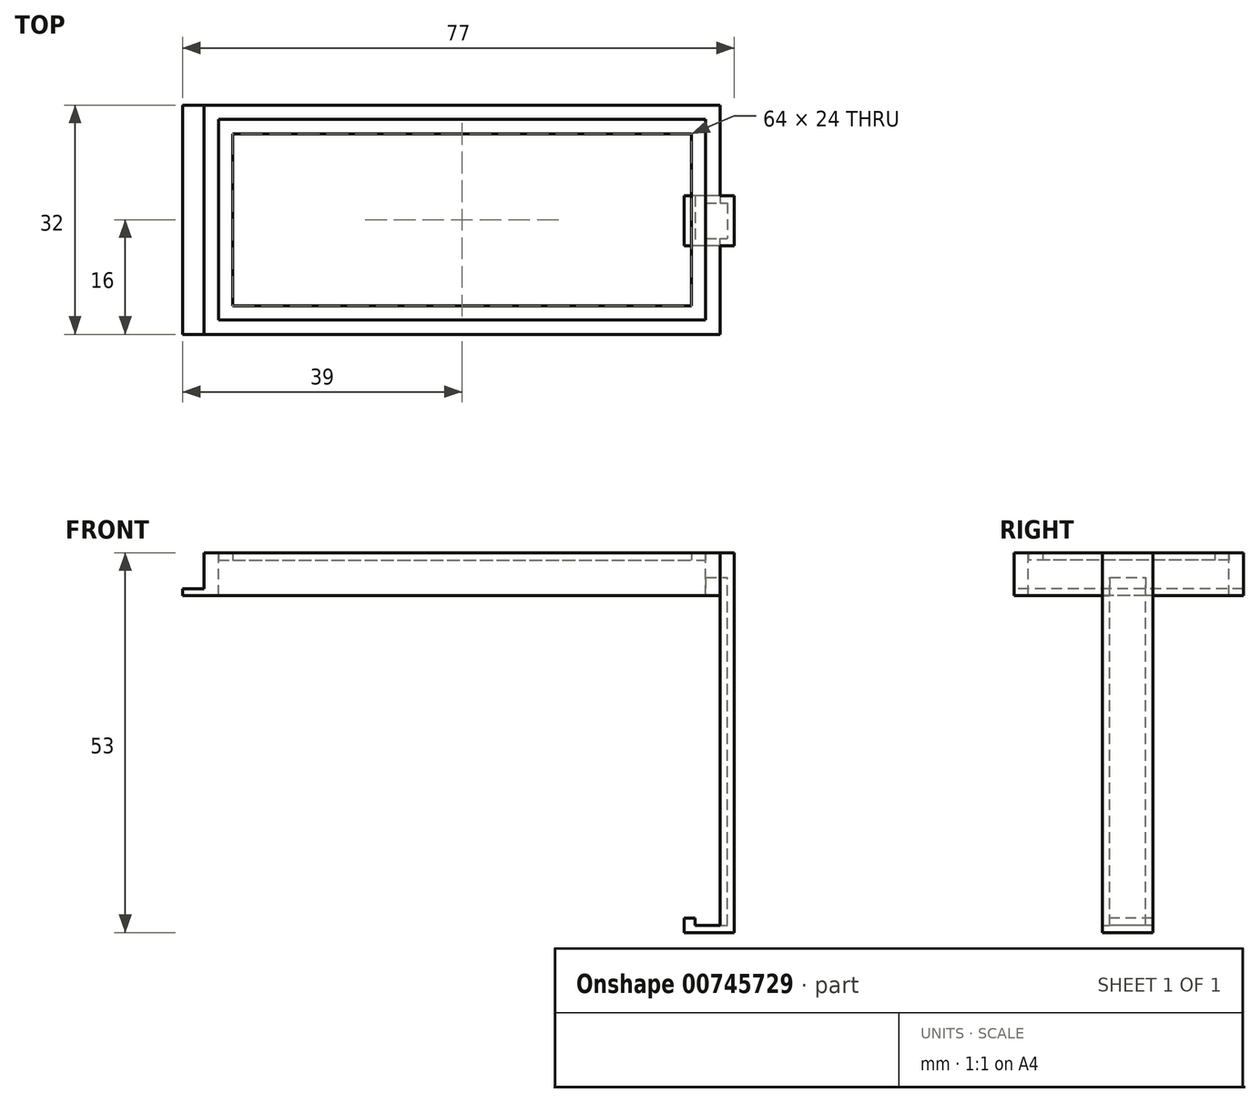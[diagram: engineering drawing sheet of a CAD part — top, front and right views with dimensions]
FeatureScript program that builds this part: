
annotation { "Feature Type Name" : "Feature", "Feature Type Description" : "" }
export const myFeature = defineFeature(function(context is Context, id is Id, definition is map)
    precondition{}
    {
        {
            var Q0;
            Q0=qCreatedBy(makeId("Top.planeOp"),FACE);
            var sketch = newSketch(context, id + "F0", { "sketchPlane" : qUnion([Q0])});
            skLineSegment(sketch, "E0.bottom", {"start": v(-32, 12) * mm, "end": v(32, 12) * mm});
            skLineSegment(sketch, "E0.top", {"start": v(-32, -12) * mm, "end": v(32, -12) * mm});
            skLineSegment(sketch, "E0.left", {"start": v(-32, 12) * mm, "end": v(-32, -12) * mm});
            skLineSegment(sketch, "E0.right", {"start": v(32, 12) * mm, "end": v(32, -12) * mm});
            skPoint(sketch, "E0.middle", {"position": v(0, 0) * mm});
            skLineSegment(sketch, "E1.0", {"start": v(-34, 14) * mm, "end": v(34, 14) * mm});
            skLineSegment(sketch, "E1.1", {"start": v(-34, 14) * mm, "end": v(-34, -14) * mm});
            skLineSegment(sketch, "E1.2", {"start": v(-34, -14) * mm, "end": v(34, -14) * mm});
            skLineSegment(sketch, "E1.3", {"start": v(34, 14) * mm, "end": v(34, -14) * mm});
            skSolve(sketch);
        }
        {
            var Q0;
            Q0=makeQuery(id+"F0.imprint","IMPRINT",FACE,{"disambiguationData":[TD([[makeQuery(id+"F0.imprint","IMPRINT",EDGE,{"derivedFrom":sQuery(id+"F0.wireOp",EDGE,"E0.bottom")}),1.0]])]});
            extrude(context, id + "F1", {"entities" : qUnion([Q0]), "depth" : 1 * mm, "offsetDistance" : 25 * mm});
        }
        {
            var Q0;
            Q0=makeQuery(id+"F1.opExtrude","CAP_FACE",FACE,{"disambiguationData":[OSD([sQuery(id+"F0.wireOp",EDGE,"E0.bottom"),sQuery(id+"F0.wireOp",EDGE,"E0.top"),sQuery(id+"F0.wireOp",EDGE,"E0.left"),sQuery(id+"F0.wireOp",EDGE,"E0.right"),sQuery(id+"F0.wireOp",EDGE,"E1.0"),sQuery(id+"F0.wireOp",EDGE,"E1.1"),sQuery(id+"F0.wireOp",EDGE,"E1.2"),sQuery(id+"F0.wireOp",EDGE,"E1.3")])],"isStart":false});
            var sketch = newSketch(context, id + "F2", { "sketchPlane" : qUnion([Q0])});
            skLineSegment(sketch, "E2.0", {"start": v(36, 16) * mm, "end": v(36, -16) * mm});
            skLineSegment(sketch, "E2.1", {"start": v(-36, 16) * mm, "end": v(36, 16) * mm});
            skLineSegment(sketch, "E2.2", {"start": v(-36, 16) * mm, "end": v(-36, -16) * mm});
            skLineSegment(sketch, "E2.3", {"start": v(-36, -16) * mm, "end": v(36, -16) * mm});
            skSolve(sketch);
        }
        {
            var Q0;
            Q0=makeQuery(id+"F2.imprint","IMPRINT",FACE,{"disambiguationData":[TD([[makeQuery(id+"F2.imprint","IMPRINT",EDGE,{"derivedFrom":sQuery(id+"F2.wireOp",EDGE,"E2.0")}),-1.0]])]});
            extrude(context, id + "F3", {"entities" : qUnion([Q0]), "oppositeDirection" : true, "depth" : 6 * mm, "offsetDistance" : 25 * mm});
        }
        {
            var Q0;
            Q0=makeQuery(id+"F3.opExtrude","SWEPT_FACE",FACE,{"disambiguationData":[OSD([sQuery(id+"F2.wireOp",EDGE,"E2.0")])]});
            var sketch = newSketch(context, id + "F4", { "sketchPlane" : qUnion([Q0])});
            skLineSegment(sketch, "E3.bottom", {"start": v(-2.65, -5) * mm, "end": v(2.35, -5) * mm});
            skLineSegment(sketch, "E3.top", {"start": v(-2.65, -2.44) * mm, "end": v(2.35, -2.44) * mm});
            skLineSegment(sketch, "E3.left", {"start": v(-2.65, -5) * mm, "end": v(-2.65, -2.44) * mm});
            skLineSegment(sketch, "E3.right", {"start": v(2.35, -5) * mm, "end": v(2.35, -2.44) * mm});
            skSolve(sketch);
        }
        {
            var Q0;
            Q0=makeQuery(id+"F4.imprint","IMPRINT",FACE,{"disambiguationData":[TD([[makeQuery(id+"F4.imprint","IMPRINT",EDGE,{"derivedFrom":sQuery(id+"F4.wireOp",EDGE,"E3.bottom")}),-1.0]])]});
            extrude(context, id + "F5", {"entities" : qUnion([Q0]), "operationType" : NewBodyOperationType.REMOVE, "oppositeDirection" : true, "depth" : 3 * mm, "offsetDistance" : 25 * mm});
        }
        {
            var Q0;
            Q0=makeQuery(id+"F3.opExtrude","SWEPT_FACE",FACE,{"disambiguationData":[OSD([sQuery(id+"F2.wireOp",EDGE,"E2.0")])]});
            var sketch = newSketch(context, id + "F6", { "sketchPlane" : qUnion([Q0])});
            skLineSegment(sketch, "E4.0", {"start": v(-3.65, -5) * mm, "end": v(-3.65, -1.44) * mm});
            skLineSegment(sketch, "E4.1", {"start": v(-3.65, -1.44) * mm, "end": v(3.35, -1.44) * mm});
            skLineSegment(sketch, "E4.2", {"start": v(3.35, -5) * mm, "end": v(3.35, -1.44) * mm});
            skSolve(sketch);
        }
        {
            var Q0;
            {var subQ10=sQuery(id+"F6.wireOp",EDGE,"E4.0");Q0=makeQuery(id+"F6.imprint","IMPRINT",FACE,{"disambiguationData":[TD([[makeQuery(id+"F6.imprint","IMPRINT",EDGE,{"derivedFrom":subQ10}),-1.0]])]});}
            extrude(context, id + "F7", {"entities" : qUnion([Q0]), "operationType" : NewBodyOperationType.ADD, "depth" : 2 * mm, "offsetDistance" : 25 * mm});
        }
        {
            var Q0;
            {var subQ0=sQuery(id+"F2.wireOp",EDGE,"E2.0");var subQ2=sQuery(id+"F2.wireOp",EDGE,"E2.3");var subQ3=sQuery(id+"F2.wireOp",EDGE,"E2.1");var subQ4=makeQuery(id+"F3.opExtrude","CAP_FACE",FACE,{"disambiguationData":[OSD([sQuery(id+"F0.wireOp",EDGE,"E1.0"),sQuery(id+"F0.wireOp",EDGE,"E1.1"),sQuery(id+"F0.wireOp",EDGE,"E1.2"),sQuery(id+"F0.wireOp",EDGE,"E1.3"),subQ0,subQ3,sQuery(id+"F2.wireOp",EDGE,"E2.2"),subQ2])],"isStart":false});var subQ5=sQuery(id+"F4.wireOp",EDGE,"E3.left");var subQ6=makeQuery(id+"F3.opExtrude","CAP_EDGE",EDGE,{"disambiguationData":[OSD([subQ0])],"isStart":false});var subQ7=makeQuery(id+"F5.boolean.opBoolean","SPLIT",EDGE,{"disambiguationData":[TD([makeQuery(id+"F3.opExtrude","SWEPT_FACE",FACE,{"disambiguationData":[OSD([subQ2])]})])],"derivedFrom":subQ6});var subQ8=sQuery(id+"F4.wireOp",EDGE,"E3.right");var subQ9=makeQuery(id+"F5.boolean.opBoolean","SPLIT",EDGE,{"disambiguationData":[TD([makeQuery(id+"F3.opExtrude","SWEPT_FACE",FACE,{"disambiguationData":[OSD([subQ3])]})])],"derivedFrom":subQ6});Q0=makeQuery(id+"F7.boolean.opBoolean","MERGE",FACE,{"derivedFrom":[subQ4,makeQuery(id+"F7.opExtrude","SWEPT_FACE",FACE,{"disambiguationData":[OSD([subQ0]),TDD([makeQuery(id+"F6.imprint","IMPRINT",EDGE,{"disambiguationData":[TD([[makeQuery(id+"F6.imprint","INTERSECT",VERTEX,{"derivedFrom":[makeQuery(id+"F5.boolean.opBoolean","COPY",EDGE,{"derivedFrom":makeQuery(id+"F5.opExtrude","CAP_EDGE",EDGE,{"disambiguationData":[OSD([subQ8])],"isStart":true})}),subQ9]}),1.0]])],"derivedFrom":subQ9})])]}),makeQuery(id+"F7.opExtrude","SWEPT_FACE",FACE,{"disambiguationData":[OSD([subQ0]),TDD([makeQuery(id+"F6.imprint","IMPRINT",EDGE,{"disambiguationData":[TD([[makeQuery(id+"F6.imprint","INTERSECT",VERTEX,{"derivedFrom":[makeQuery(id+"F5.boolean.opBoolean","COPY",EDGE,{"derivedFrom":makeQuery(id+"F5.opExtrude","CAP_EDGE",EDGE,{"disambiguationData":[OSD([subQ5])],"isStart":true})}),subQ7]}),-1.0]])],"derivedFrom":subQ7})])]})]});}
            var sketch = newSketch(context, id + "F8", { "sketchPlane" : qUnion([Q0])});
            skLineSegment(sketch, "E5.bottom", {"start": v(36, -3.35) * mm, "end": v(38, -3.35) * mm});
            skLineSegment(sketch, "E5.top", {"start": v(36, -2.35) * mm, "end": v(38, -2.35) * mm});
            skLineSegment(sketch, "E5.left", {"start": v(36, -3.35) * mm, "end": v(36, -2.35) * mm});
            skLineSegment(sketch, "E5.right", {"start": v(38, -3.35) * mm, "end": v(38, -2.35) * mm});
            skLineSegment(sketch, "E6.bottom", {"start": v(36, 3.65) * mm, "end": v(38, 3.65) * mm});
            skLineSegment(sketch, "E6.top", {"start": v(36, 2.65) * mm, "end": v(38, 2.65) * mm});
            skLineSegment(sketch, "E6.left", {"start": v(36, 3.65) * mm, "end": v(36, 2.65) * mm});
            skLineSegment(sketch, "E6.right", {"start": v(38, 3.65) * mm, "end": v(38, 2.65) * mm});
            skLineSegment(sketch, "E7.bottom", {"start": v(38, -2.35) * mm, "end": v(37, -2.35) * mm});
            skLineSegment(sketch, "E7.top", {"start": v(38, 2.65) * mm, "end": v(37, 2.65) * mm});
            skLineSegment(sketch, "E7.left", {"start": v(38, -2.35) * mm, "end": v(38, 2.65) * mm});
            skLineSegment(sketch, "E7.right", {"start": v(37, -2.35) * mm, "end": v(37, 2.65) * mm});
            skSolve(sketch);
        }
        {
            var Q0;
            Q0=makeQuery(id+"F8.imprint","IMPRINT",FACE,{"disambiguationData":[TD([[makeQuery(id+"F8.imprint","IMPRINT",EDGE,{"derivedFrom":sQuery(id+"F8.wireOp",EDGE,"E5.bottom")}),-1.0]])]});
            var Q1;
            Q1=makeQuery(id+"F8.imprint","IMPRINT",FACE,{"disambiguationData":[TD([[makeQuery(id+"F8.imprint","IMPRINT",EDGE,{"derivedFrom":sQuery(id+"F8.wireOp",EDGE,"E6.bottom")}),1.0]])]});
            extrude(context, id + "F9", {"entities" : qUnion([Q0, Q1]), "operationType" : NewBodyOperationType.ADD, "depth" : 47 * mm, "offsetDistance" : 25 * mm, "hasSecondDirection" : true, "secondDirectionOppositeDirection" : true, "secondDirectionDepth" : 6 * mm});
        }
        {
            var Q0;
            Q0 = qSketchRegion(id + "F8", true);
            extrude(context, id + "F10", {"entities" : qUnion([Q0]), "operationType" : NewBodyOperationType.ADD, "depth" : 47 * mm, "offsetDistance" : 25 * mm, "hasSecondDirection" : true, "secondDirectionOppositeDirection" : true, "secondDirectionDepth" : 6 * mm});
        }
        {
            var Q0;
            {var subQ0=sQuery(id+"F8.wireOp",EDGE,"E6.right");var subQ1=sQuery(id+"F8.wireOp",EDGE,"E6.left");var subQ2=sQuery(id+"F8.wireOp",EDGE,"E6.top");var subQ3=sQuery(id+"F8.wireOp",EDGE,"E6.bottom");var subQ4=sQuery(id+"F8.wireOp",EDGE,"E5.right");var subQ5=sQuery(id+"F8.wireOp",EDGE,"E5.left");var subQ6=sQuery(id+"F8.wireOp",EDGE,"E5.top");var subQ7=sQuery(id+"F8.wireOp",EDGE,"E5.bottom");Q0=makeQuery(id+"F10.boolean.opBoolean","MERGE",FACE,{"derivedFrom":[makeQuery(id+"F9.opExtrude","CAP_FACE",FACE,{"disambiguationData":[OSD([subQ7,subQ6,subQ5,subQ4,sQuery(id+"F8.wireOp",EDGE,"E7.bottom")])],"isStart":false}),makeQuery(id+"F9.opExtrude","CAP_FACE",FACE,{"disambiguationData":[OSD([subQ3,subQ2,subQ1,subQ0,sQuery(id+"F8.wireOp",EDGE,"E7.top")])],"isStart":false}),makeQuery(id+"F10.opExtrude","CAP_FACE",FACE,{"disambiguationData":[OSD([subQ7,subQ6,subQ5,subQ4,subQ3,subQ2,subQ1,subQ0,sQuery(id+"F8.wireOp",EDGE,"E7.left"),sQuery(id+"F8.wireOp",EDGE,"E7.right")])],"isStart":false})]});}
            var sketch = newSketch(context, id + "F11", { "sketchPlane" : qUnion([Q0])});
            skLineSegment(sketch, "E8.bottom", {"start": v(38, -3.35) * mm, "end": v(31, -3.35) * mm});
            skLineSegment(sketch, "E8.top", {"start": v(38, 3.65) * mm, "end": v(31, 3.65) * mm});
            skLineSegment(sketch, "E8.left", {"start": v(38, -3.35) * mm, "end": v(38, 3.65) * mm});
            skLineSegment(sketch, "E8.right", {"start": v(31, -3.35) * mm, "end": v(31, 3.65) * mm});
            skSolve(sketch);
        }
        {
            var Q0;
            {var subQ3=sQuery(id+"F11.wireOp",EDGE,"E8.right");Q0=makeQuery(id+"F11.imprint","IMPRINT",FACE,{"disambiguationData":[TD([[makeQuery(id+"F11.imprint","IMPRINT",EDGE,{"derivedFrom":subQ3}),-1.0]])]});}
            extrude(context, id + "F12", {"entities" : qUnion([Q0]), "operationType" : NewBodyOperationType.ADD, "oppositeDirection" : true, "depth" : 1 * mm, "offsetDistance" : 25 * mm});
        }
        {
            var Q0;
            Q0=makeQuery(id+"F12.opExtrude","CAP_FACE",FACE,{"disambiguationData":[OSD([sQuery(id+"F8.wireOp",EDGE,"E5.top"),sQuery(id+"F8.wireOp",EDGE,"E5.left"),sQuery(id+"F8.wireOp",EDGE,"E6.top"),sQuery(id+"F8.wireOp",EDGE,"E6.left"),sQuery(id+"F8.wireOp",EDGE,"E7.bottom"),sQuery(id+"F8.wireOp",EDGE,"E7.top"),sQuery(id+"F8.wireOp",EDGE,"E7.right"),sQuery(id+"F11.wireOp",EDGE,"E8.bottom"),sQuery(id+"F11.wireOp",EDGE,"E8.top"),sQuery(id+"F11.wireOp",EDGE,"E8.right")])],"isStart":false});
            var sketch = newSketch(context, id + "F13", { "sketchPlane" : qUnion([Q0])});
            skLineSegment(sketch, "E9.bottom", {"start": v(31, 3.35) * mm, "end": v(32.5, 3.35) * mm});
            skLineSegment(sketch, "E9.top", {"start": v(31, -3.65) * mm, "end": v(32.5, -3.65) * mm});
            skLineSegment(sketch, "E9.left", {"start": v(31, 3.35) * mm, "end": v(31, -3.65) * mm});
            skLineSegment(sketch, "E9.right", {"start": v(32.5, 3.35) * mm, "end": v(32.5, -3.65) * mm});
            skSolve(sketch);
        }
        {
            var Q0;
            Q0=makeQuery(id+"F13.imprint","IMPRINT",FACE,{"disambiguationData":[TD([[makeQuery(id+"F13.imprint","IMPRINT",EDGE,{"derivedFrom":sQuery(id+"F13.wireOp",EDGE,"E9.bottom")}),1.0]])]});
            extrude(context, id + "F14", {"entities" : qUnion([Q0]), "operationType" : NewBodyOperationType.ADD, "depth" : 1 * mm, "offsetDistance" : 25 * mm});
        }
        {
            var Q0;
            Q0=makeQuery(id+"F7.opExtrude","SWEPT_FACE",FACE,{"disambiguationData":[OSD([sQuery(id+"F6.wireOp",EDGE,"E4.1")])]});
            extrude(context, id + "F15", {"entities" : qUnion([Q0]), "operationType" : NewBodyOperationType.ADD, "depth" : 2.45 * mm, "offsetDistance" : 25 * mm});
        }
        {
            var Q0;
            Q0=makeQuery(id+"F3.opExtrude","SWEPT_FACE",FACE,{"disambiguationData":[OSD([sQuery(id+"F2.wireOp",EDGE,"E2.2")])]});
            var sketch = newSketch(context, id + "F16", { "sketchPlane" : qUnion([Q0])});
            skLineSegment(sketch, "E10.bottom", {"start": v(-16, -5) * mm, "end": v(16, -5) * mm});
            skLineSegment(sketch, "E10.top", {"start": v(-16, -4) * mm, "end": v(16, -4) * mm});
            skLineSegment(sketch, "E10.left", {"start": v(-16, -5) * mm, "end": v(-16, -4) * mm});
            skLineSegment(sketch, "E10.right", {"start": v(16, -5) * mm, "end": v(16, -4) * mm});
            skSolve(sketch);
        }
        {
            var Q0;
            Q0=makeQuery(id+"F16.imprint","IMPRINT",FACE,{"disambiguationData":[TD([[makeQuery(id+"F16.imprint","IMPRINT",EDGE,{"derivedFrom":sQuery(id+"F16.wireOp",EDGE,"E10.bottom")}),1.0]])]});
            extrude(context, id + "F17", {"entities" : qUnion([Q0]), "operationType" : NewBodyOperationType.ADD, "depth" : 3 * mm, "offsetDistance" : 25 * mm});
        }
    });
